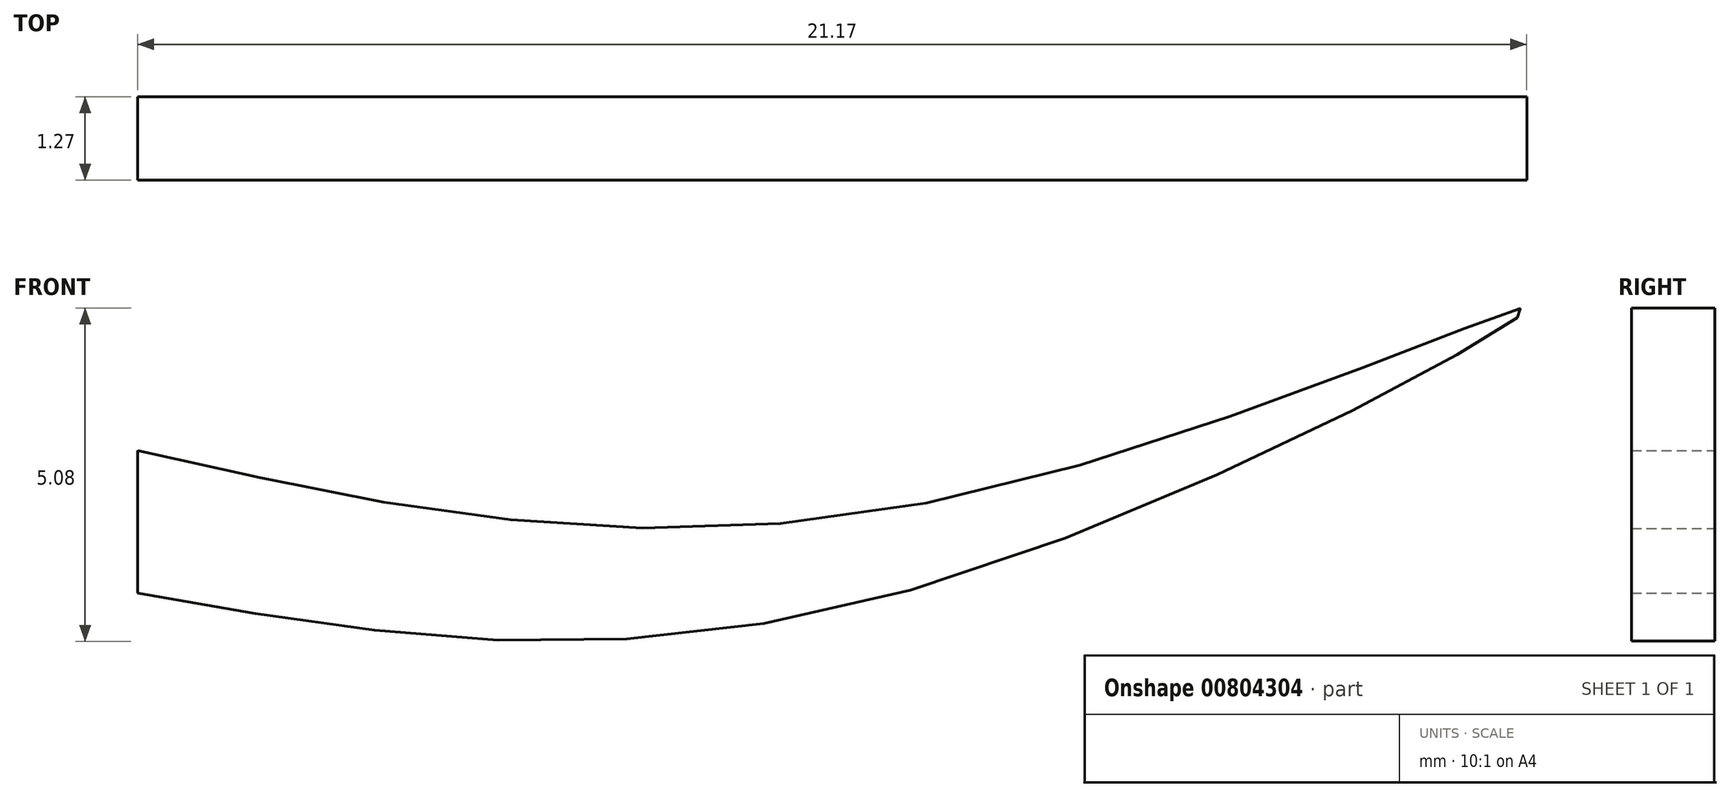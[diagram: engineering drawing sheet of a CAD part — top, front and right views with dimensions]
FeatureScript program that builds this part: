
annotation { "Feature Type Name" : "Feature", "Feature Type Description" : "" }
export const myFeature = defineFeature(function(context is Context, id is Id, definition is map)
    precondition{}
    {
        {
            var Q0;
            Q0=qCreatedBy(makeId("Front.planeOp"),FACE);
            var sketch = newSketch(context, id + "F0", { "sketchPlane" : qUnion([Q0])});
            skLineSegment(sketch, "E0", {"start": v(0, 0.37) * mm, "end": v(0, -2.17) * mm});
            skFitSpline(sketch, "E1", {"points": [v(0, -2.17) * mm, v(11.62, -2.17) * mm, v(21.17, 2.16) * mm, v(12.24, -0.76) * mm, v(0, 0) * mm], "startDerivative": vector(41.06, -7.39) * mm, "endDerivative": vector(-42.78, 9.78) * mm});
            skSolve(sketch);
        }
        {
            var Q0;
            {var subQ0=sQuery(id+"F0.wireOp",EDGE,"E1");Q0=makeQuery(id+"F0.imprint","IMPRINT",FACE,{"disambiguationData":[TD([[makeQuery(id+"F0.imprint","IMPRINT",EDGE,{"derivedFrom":subQ0}),1.0]])]});}
            extrude(context, id + "F1", {"entities" : qUnion([Q0]), "depth" : 1.27 * mm, "offsetDistance" : 25.4 * mm});
        }
    });
